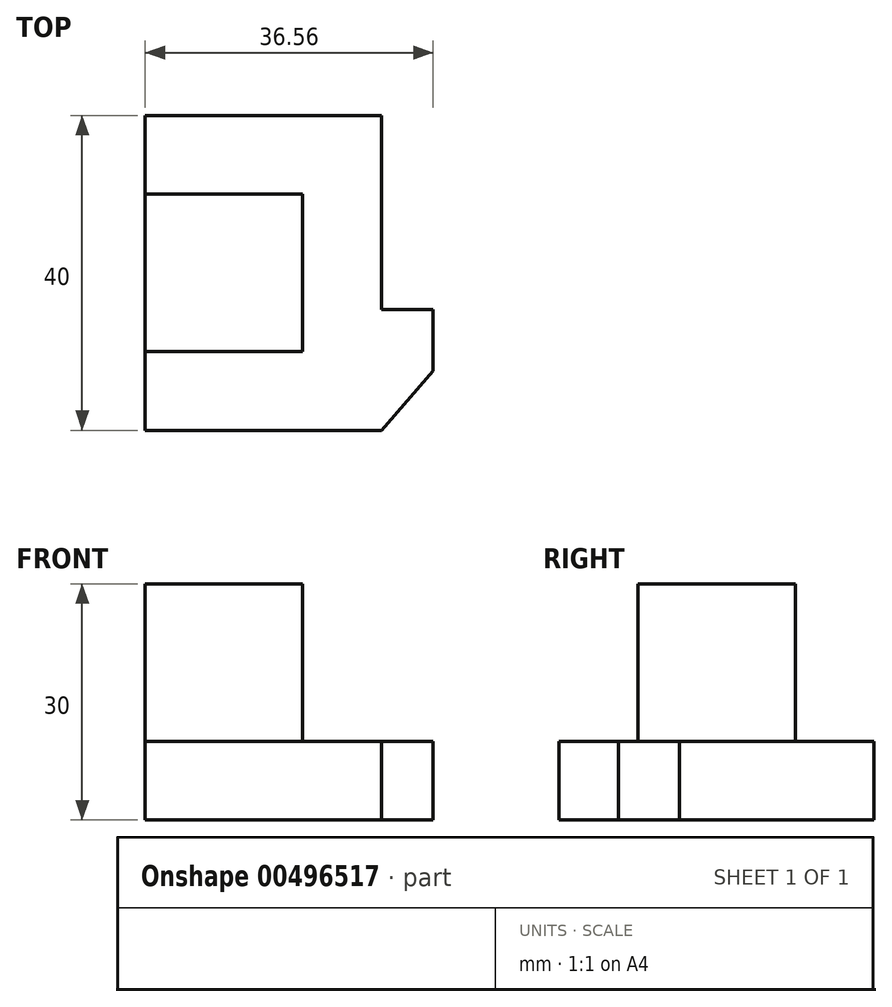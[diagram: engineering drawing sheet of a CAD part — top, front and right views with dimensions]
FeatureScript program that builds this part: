
annotation { "Feature Type Name" : "Feature", "Feature Type Description" : "" }
export const myFeature = defineFeature(function(context is Context, id is Id, definition is map)
    precondition{}
    {
        {
            var Q0;
            Q0=qCreatedBy(makeId("Top.planeOp"),FACE);
            var sketch = newSketch(context, id + "F0", { "sketchPlane" : qUnion([Q0])});
            skLineSegment(sketch, "E0", {"start": v(0, 0) * mm, "end": v(0, 40) * mm});
            skLineSegment(sketch, "E1", {"start": v(0, 40) * mm, "end": v(30, 40) * mm});
            skLineSegment(sketch, "E2", {"start": v(0, 0) * mm, "end": v(30, 0) * mm});
            skLineSegment(sketch, "E3", {"start": v(30, 0) * mm, "end": v(36.56, 7.55) * mm});
            skLineSegment(sketch, "E4", {"start": v(36.56, 7.55) * mm, "end": v(36.56, 15.32) * mm});
            skLineSegment(sketch, "E5", {"start": v(30, 40) * mm, "end": v(30, 15.32) * mm});
            skLineSegment(sketch, "E6", {"start": v(30, 15.32) * mm, "end": v(36.56, 15.32) * mm});
            skSolve(sketch);
        }
        {
            var Q0;
            Q0 = qSketchRegion(id + "F0", true);
            extrude(context, id + "F1", {"entities" : qUnion([Q0]), "depth" : 10 * mm});
        }
        {
            var Q0;
            Q0=makeQuery(id+"F1.opExtrude","CAP_FACE",FACE,{"disambiguationData":[OSD([sQuery(id+"F0.wireOp",EDGE,"E0"),sQuery(id+"F0.wireOp",EDGE,"E1"),sQuery(id+"F0.wireOp",EDGE,"E2"),sQuery(id+"F0.wireOp",EDGE,"E3"),sQuery(id+"F0.wireOp",EDGE,"E4"),sQuery(id+"F0.wireOp",EDGE,"E5"),sQuery(id+"F0.wireOp",EDGE,"E6")])],"isStart":false});
            var sketch = newSketch(context, id + "F2", { "sketchPlane" : qUnion([Q0])});
            skLineSegment(sketch, "E7", {"start": v(0, 0) * mm, "end": v(0, 30) * mm});
            skLineSegment(sketch, "E8", {"start": v(0, 30) * mm, "end": v(20, 30) * mm});
            skLineSegment(sketch, "E9", {"start": v(20, 30) * mm, "end": v(20, 10) * mm});
            skLineSegment(sketch, "E10", {"start": v(20, 10) * mm, "end": v(0, 10) * mm});
            skSolve(sketch);
        }
        {
            var Q0;
            Q0 = qSketchRegion(id + "F2", true);
            extrude(context, id + "F3", {"entities" : qUnion([Q0]), "operationType" : NewBodyOperationType.ADD, "depth" : 20 * mm});
        }
    });
